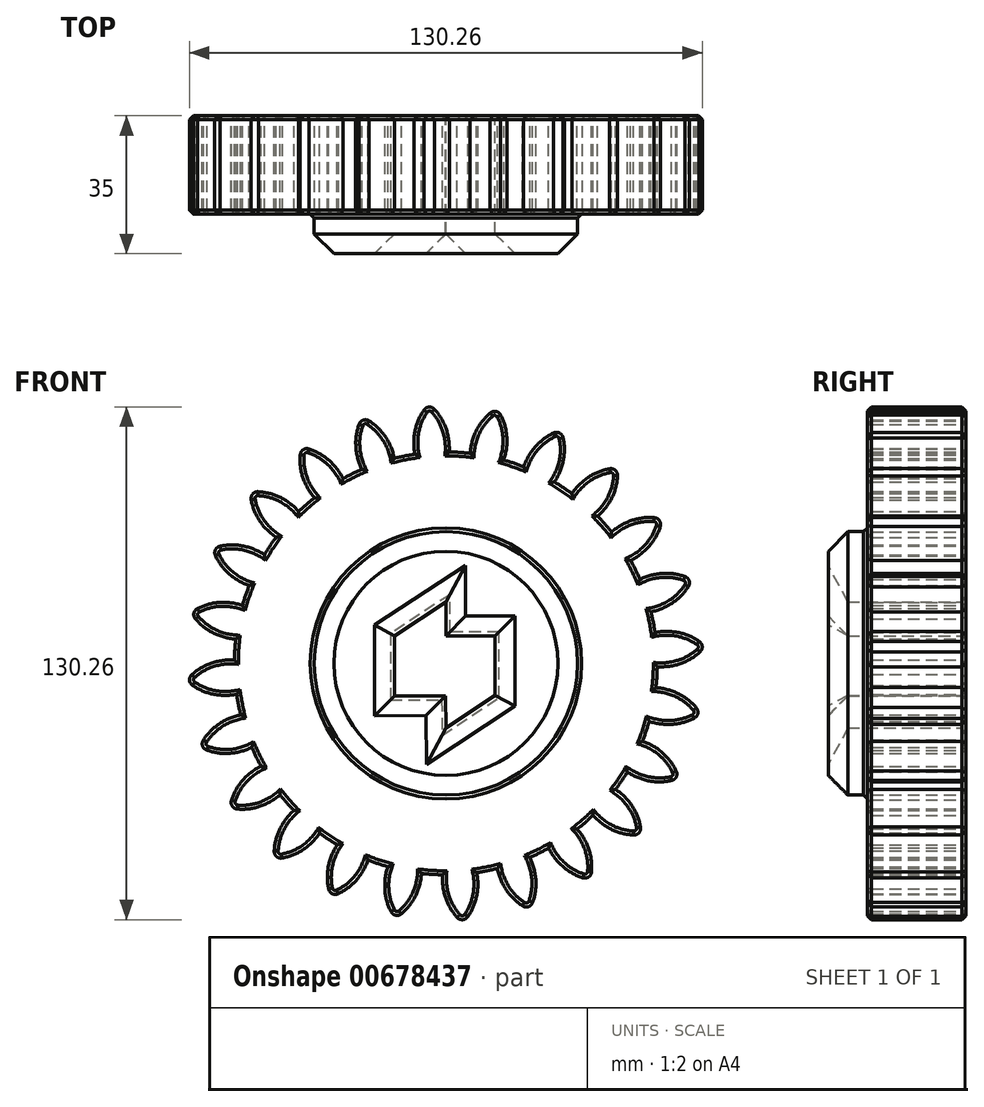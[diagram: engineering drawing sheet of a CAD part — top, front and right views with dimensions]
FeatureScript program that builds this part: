
annotation { "Feature Type Name" : "Feature", "Feature Type Description" : "" }
export const myFeature = defineFeature(function(context is Context, id is Id, definition is map)
    precondition{}
    {
        {
            var Q0;
            Q0=qCreatedBy(makeId("Front.planeOp"),FACE);
            var sketch = newSketch(context, id + "F0", { "sketchPlane" : qUnion([Q0])});
            skCircle(sketch, "E0", {"center": v(0, 1.08) * mm, "radius": 58.67 * mm, "construction": true});
            skCircle(sketch, "E1", {"center": v(0, 1.08) * mm, "radius": 63.5 * mm, "construction": true});
            skCircle(sketch, "E2", {"center": v(0, 0) * mm, "radius": 53.72 * mm});
            skLineSegment(sketch, "E3", {"start": v(0, 0) * mm, "end": v(-5.31, 81.05) * mm, "construction": true});
            skLineSegment(sketch, "E4", {"start": v(0, 59.76) * mm, "end": v(-52.82, 59.76) * mm, "construction": true});
            skLineSegment(sketch, "E5", {"start": v(0, 59.76) * mm, "end": v(-56.13, 39.33) * mm, "construction": true});
            skCircle(sketch, "E6", {"center": v(0, 1.08) * mm, "radius": 55.14 * mm, "construction": true});
            skCircle(sketch, "E7", {"center": v(0, 59.76) * mm, "radius": 14.6 * mm, "construction": true});
            skCircle(sketch, "E8", {"center": v(-13.72, 54.76) * mm, "radius": 14.6 * mm, "construction": true});
            skArc(sketch, "E9", {"start": v(0, 59.76) * mm, "mid": v(-1.2, 62.28) * mm, "end": v(-2.86, 64.52) * mm});
            skArc(sketch, "E10", {"start": v(0.84, 53.71) * mm, "mid": v(0.73, 56.78) * mm, "end": v(0, 59.76) * mm});
            skArc(sketch, "E11.MirrorCS", {"start": v(-7.8, 59.25) * mm, "mid": v(-6.95, 61.9) * mm, "end": v(-5.59, 64.34) * mm});
            skArc(sketch, "E12.MirrorCS", {"start": v(-7.85, 53.14) * mm, "mid": v(-8.13, 56.2) * mm, "end": v(-7.8, 59.25) * mm});
            skArc(sketch, "E13", {"start": v(-2.86, 64.52) * mm, "mid": v(-4.27, 65.13) * mm, "end": v(-5.59, 64.34) * mm});
            skCircle(sketch, "E14", {"center": v(0, 0) * mm, "radius": 33.45 * mm});
            skLineSegment(sketch, "E15", {"start": v(-13.1, 7) * mm, "end": v(-13.1, -8.32) * mm});
            skLineSegment(sketch, "E16", {"start": v(-13.1, 7) * mm, "end": v(12.53, 7) * mm});
            skLineSegment(sketch, "E17", {"start": v(12.53, 7) * mm, "end": v(12.53, -8.13) * mm});
            skLineSegment(sketch, "E18", {"start": v(12.53, -8.13) * mm, "end": v(-13.1, -8.32) * mm});
            skLineSegment(sketch, "E19", {"start": v(-13.1, 7) * mm, "end": v(0, 15.58) * mm});
            skLineSegment(sketch, "E20", {"start": v(0, 15.58) * mm, "end": v(0, 7) * mm});
            skLineSegment(sketch, "E21", {"start": v(12.53, -8.13) * mm, "end": v(0, -16.43) * mm});
            skLineSegment(sketch, "E22", {"start": v(0, -16.43) * mm, "end": v(-0.06, -8.13) * mm});
            skSolve(sketch);
        }
        {
            var Q0;
            {var subQ0=sQuery(id+"F0.wireOp",EDGE,"E2");var subQ1=makeQuery(id+"F0.imprint","INTERSECT",VERTEX,{"derivedFrom":[subQ0,sQuery(id+"F0.wireOp",EDGE,"E10")]});Q0=makeQuery(id+"F0.imprint","IMPRINT",FACE,{"disambiguationData":[TD([[makeQuery(id+"F0.imprint","IMPRINT",EDGE,{"disambiguationData":[TD([[subQ1,-1.0]])],"derivedFrom":subQ0}),1.0]])]});}
            var Q1;
            Q1=makeQuery(id+"F0.imprint","IMPRINT",FACE,{"disambiguationData":[TD([[makeQuery(id+"F0.imprint","IMPRINT",EDGE,{"derivedFrom":sQuery(id+"F0.wireOp",EDGE,"E9")}),1.0]])]});
            extrude(context, id + "F1", {"entities" : qUnion([Q0, Q1]), "depth" : 25 * mm, "offsetDistance" : 25 * mm});
        }
        {
            var Q0;
            Q0=makeQuery(id+"F1.opExtrude","SWEPT_BODY",BODY,{"disambiguationData":[OSD([sQuery(id+"F0.wireOp",EDGE,"E2"),sQuery(id+"F0.wireOp",EDGE,"E9"),sQuery(id+"F0.wireOp",EDGE,"E10"),sQuery(id+"F0.wireOp",EDGE,"E11.MirrorCS"),sQuery(id+"F0.wireOp",EDGE,"E12.MirrorCS"),sQuery(id+"F0.wireOp",EDGE,"E13")])]});
            var Q1;
            Q1=makeQuery(id+"F1.opExtrude","SWEPT_FACE",FACE,{"disambiguationData":[OSD([sQuery(id+"F0.wireOp",EDGE,"E2")])]});
            circularPattern(context, id + "F2", {"entities" : qUnion([Q0]), "axis" : qUnion([Q1]), "angle" : 360 * degree, "instanceCount" : 24, "equalSpace" : true});
        }
        {
            var Q0;
            Q0=makeQuery(id+"F0.imprint","IMPRINT",FACE,{"disambiguationData":[TD([[makeQuery(id+"F0.imprint","IMPRINT",EDGE,{"derivedFrom":sQuery(id+"F0.wireOp",EDGE,"E14")}),1.0]])]});
            extrude(context, id + "F3", {"entities" : qUnion([Q0]), "operationType" : NewBodyOperationType.ADD, "depth" : 35 * mm, "offsetDistance" : 25 * mm});
        }
        {
            var Q0;
            Q0=makeQuery(id+"F3.opExtrude","CAP_FACE",FACE,{"disambiguationData":[OSD([sQuery(id+"F0.wireOp",EDGE,"E14"),sQuery(id+"F0.wireOp",EDGE,"VNX0vvCv-WYPK-WpQ4-Qnou-ul3imrYvSMJw.bottom"),sQuery(id+"F0.wireOp",EDGE,"VNX0vvCv-WYPK-WpQ4-Qnou-ul3imrYvSMJw.top"),sQuery(id+"F0.wireOp",EDGE,"VNX0vvCv-WYPK-WpQ4-Qnou-ul3imrYvSMJw.left"),sQuery(id+"F0.wireOp",EDGE,"VNX0vvCv-WYPK-WpQ4-Qnou-ul3imrYvSMJw.right"),sQuery(id+"F0.wireOp",EDGE,"IJ5EXvum-596H-XTGL-SE43-JUN5fCkBIpPC"),sQuery(id+"F0.wireOp",EDGE,"IlY7Gg9C-VGWR-PZbE-QeL8-64zVfxDiq93t"),sQuery(id+"F0.wireOp",EDGE,"WuA3GpO8-G2sd-kQCD-f2T7-r0WvZ8Gg5E8L"),sQuery(id+"F0.wireOp",EDGE,"KlxLDr8O-HS7y-gG5N-Xxws-Bgi8SKMNfG0f")])],"isStart":false});
            chamfer(context, id + "F4", {"entities" : qUnion([Q0]), "width" : 5 * mm, "tangentPropagation" : true});
        }
        {
            var Q0;
            {var subQ0=makeQuery(id+"F1.opExtrude","CAP_FACE",FACE,{"disambiguationData":[OSD([sQuery(id+"F0.wireOp",EDGE,"E2"),sQuery(id+"F0.wireOp",EDGE,"E9"),sQuery(id+"F0.wireOp",EDGE,"E10"),sQuery(id+"F0.wireOp",EDGE,"E11.MirrorCS"),sQuery(id+"F0.wireOp",EDGE,"E12.MirrorCS"),sQuery(id+"F0.wireOp",EDGE,"E13"),sQuery(id+"F0.wireOp",EDGE,"E14")])],"isStart":false});Q0=makeQuery(id+"F3.boolean.opBoolean","MERGE",FACE,{"derivedFrom":[subQ0,makeQuery(id+"F2.opPattern","COPY",FACE,{"derivedFrom":subQ0,"instanceName":"1"}),makeQuery(id+"F2.opPattern","COPY",FACE,{"derivedFrom":subQ0,"instanceName":"2"}),makeQuery(id+"F2.opPattern","COPY",FACE,{"derivedFrom":subQ0,"instanceName":"3"}),makeQuery(id+"F2.opPattern","COPY",FACE,{"derivedFrom":subQ0,"instanceName":"4"}),makeQuery(id+"F2.opPattern","COPY",FACE,{"derivedFrom":subQ0,"instanceName":"5"}),makeQuery(id+"F2.opPattern","COPY",FACE,{"derivedFrom":subQ0,"instanceName":"6"}),makeQuery(id+"F2.opPattern","COPY",FACE,{"derivedFrom":subQ0,"instanceName":"7"}),makeQuery(id+"F2.opPattern","COPY",FACE,{"derivedFrom":subQ0,"instanceName":"8"}),makeQuery(id+"F2.opPattern","COPY",FACE,{"derivedFrom":subQ0,"instanceName":"9"}),makeQuery(id+"F2.opPattern","COPY",FACE,{"derivedFrom":subQ0,"instanceName":"10"}),makeQuery(id+"F2.opPattern","COPY",FACE,{"derivedFrom":subQ0,"instanceName":"11"}),makeQuery(id+"F2.opPattern","COPY",FACE,{"derivedFrom":subQ0,"instanceName":"12"}),makeQuery(id+"F2.opPattern","COPY",FACE,{"derivedFrom":subQ0,"instanceName":"13"}),makeQuery(id+"F2.opPattern","COPY",FACE,{"derivedFrom":subQ0,"instanceName":"14"}),makeQuery(id+"F2.opPattern","COPY",FACE,{"derivedFrom":subQ0,"instanceName":"15"}),makeQuery(id+"F2.opPattern","COPY",FACE,{"derivedFrom":subQ0,"instanceName":"16"}),makeQuery(id+"F2.opPattern","COPY",FACE,{"derivedFrom":subQ0,"instanceName":"17"}),makeQuery(id+"F2.opPattern","COPY",FACE,{"derivedFrom":subQ0,"instanceName":"18"}),makeQuery(id+"F2.opPattern","COPY",FACE,{"derivedFrom":subQ0,"instanceName":"19"}),makeQuery(id+"F2.opPattern","COPY",FACE,{"derivedFrom":subQ0,"instanceName":"20"}),makeQuery(id+"F2.opPattern","COPY",FACE,{"derivedFrom":subQ0,"instanceName":"21"}),makeQuery(id+"F2.opPattern","COPY",FACE,{"derivedFrom":subQ0,"instanceName":"22"}),makeQuery(id+"F2.opPattern","COPY",FACE,{"derivedFrom":subQ0,"instanceName":"23"})]});}
            var Q1;
            {var subQ0=sQuery(id+"F0.wireOp",EDGE,"E14");var subQ1=makeQuery(id+"F1.opExtrude","CAP_FACE",FACE,{"disambiguationData":[OSD([sQuery(id+"F0.wireOp",EDGE,"E2"),sQuery(id+"F0.wireOp",EDGE,"E9"),sQuery(id+"F0.wireOp",EDGE,"E10"),sQuery(id+"F0.wireOp",EDGE,"E11.MirrorCS"),sQuery(id+"F0.wireOp",EDGE,"E12.MirrorCS"),sQuery(id+"F0.wireOp",EDGE,"E13"),subQ0])],"isStart":true});Q1=makeQuery(id+"F3.boolean.opBoolean","MERGE",FACE,{"derivedFrom":[subQ1,makeQuery(id+"F2.opPattern","COPY",FACE,{"derivedFrom":subQ1,"instanceName":"1"}),makeQuery(id+"F2.opPattern","COPY",FACE,{"derivedFrom":subQ1,"instanceName":"2"}),makeQuery(id+"F2.opPattern","COPY",FACE,{"derivedFrom":subQ1,"instanceName":"3"}),makeQuery(id+"F2.opPattern","COPY",FACE,{"derivedFrom":subQ1,"instanceName":"4"}),makeQuery(id+"F2.opPattern","COPY",FACE,{"derivedFrom":subQ1,"instanceName":"5"}),makeQuery(id+"F2.opPattern","COPY",FACE,{"derivedFrom":subQ1,"instanceName":"6"}),makeQuery(id+"F2.opPattern","COPY",FACE,{"derivedFrom":subQ1,"instanceName":"7"}),makeQuery(id+"F2.opPattern","COPY",FACE,{"derivedFrom":subQ1,"instanceName":"8"}),makeQuery(id+"F2.opPattern","COPY",FACE,{"derivedFrom":subQ1,"instanceName":"9"}),makeQuery(id+"F2.opPattern","COPY",FACE,{"derivedFrom":subQ1,"instanceName":"10"}),makeQuery(id+"F2.opPattern","COPY",FACE,{"derivedFrom":subQ1,"instanceName":"11"}),makeQuery(id+"F2.opPattern","COPY",FACE,{"derivedFrom":subQ1,"instanceName":"12"}),makeQuery(id+"F2.opPattern","COPY",FACE,{"derivedFrom":subQ1,"instanceName":"13"}),makeQuery(id+"F2.opPattern","COPY",FACE,{"derivedFrom":subQ1,"instanceName":"14"}),makeQuery(id+"F2.opPattern","COPY",FACE,{"derivedFrom":subQ1,"instanceName":"15"}),makeQuery(id+"F2.opPattern","COPY",FACE,{"derivedFrom":subQ1,"instanceName":"16"}),makeQuery(id+"F2.opPattern","COPY",FACE,{"derivedFrom":subQ1,"instanceName":"17"}),makeQuery(id+"F2.opPattern","COPY",FACE,{"derivedFrom":subQ1,"instanceName":"18"}),makeQuery(id+"F2.opPattern","COPY",FACE,{"derivedFrom":subQ1,"instanceName":"19"}),makeQuery(id+"F2.opPattern","COPY",FACE,{"derivedFrom":subQ1,"instanceName":"20"}),makeQuery(id+"F2.opPattern","COPY",FACE,{"derivedFrom":subQ1,"instanceName":"21"}),makeQuery(id+"F2.opPattern","COPY",FACE,{"derivedFrom":subQ1,"instanceName":"22"}),makeQuery(id+"F2.opPattern","COPY",FACE,{"derivedFrom":subQ1,"instanceName":"23"}),makeQuery(id+"F3.opExtrude","CAP_FACE",FACE,{"disambiguationData":[OSD([subQ0,sQuery(id+"F0.wireOp",EDGE,"VNX0vvCv-WYPK-WpQ4-Qnou-ul3imrYvSMJw.bottom"),sQuery(id+"F0.wireOp",EDGE,"VNX0vvCv-WYPK-WpQ4-Qnou-ul3imrYvSMJw.top"),sQuery(id+"F0.wireOp",EDGE,"VNX0vvCv-WYPK-WpQ4-Qnou-ul3imrYvSMJw.left"),sQuery(id+"F0.wireOp",EDGE,"VNX0vvCv-WYPK-WpQ4-Qnou-ul3imrYvSMJw.right"),sQuery(id+"F0.wireOp",EDGE,"IJ5EXvum-596H-XTGL-SE43-JUN5fCkBIpPC"),sQuery(id+"F0.wireOp",EDGE,"IlY7Gg9C-VGWR-PZbE-QeL8-64zVfxDiq93t"),sQuery(id+"F0.wireOp",EDGE,"WuA3GpO8-G2sd-kQCD-f2T7-r0WvZ8Gg5E8L"),sQuery(id+"F0.wireOp",EDGE,"KlxLDr8O-HS7y-gG5N-Xxws-Bgi8SKMNfG0f")])],"isStart":true})]});}
            chamfer(context, id + "F5", {"entities" : qUnion([Q0, Q1]), "width" : 1 * mm, "tangentPropagation" : true});
        }
    });
